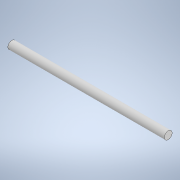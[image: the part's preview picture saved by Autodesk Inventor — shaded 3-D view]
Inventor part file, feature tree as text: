
AUTODESK INVENTOR PART (.ipt)
format: ipt  version: 2021 (Build 250183000, 183)  size: 90,624 bytes
history: native  units: in
note: dims shown in document units (in); Inventor stores cm internally (conversion verified against a paired STEP export)
features: extrude x1, sketch x1
ambient origin geometry x8: Origin, YZ Plane, XZ Plane, XY Plane, X Axis, Y Axis, Z Axis, Center Point
bodies: Solid1 (feature_tree)
feature tree (2):
  extrude  "Extrusion1"  Depth=5.0in TaperAngle=0.0deg
  sketch  "Sketch1"  dims[d0=0.25in d1=5.0in d2=0.0in]
